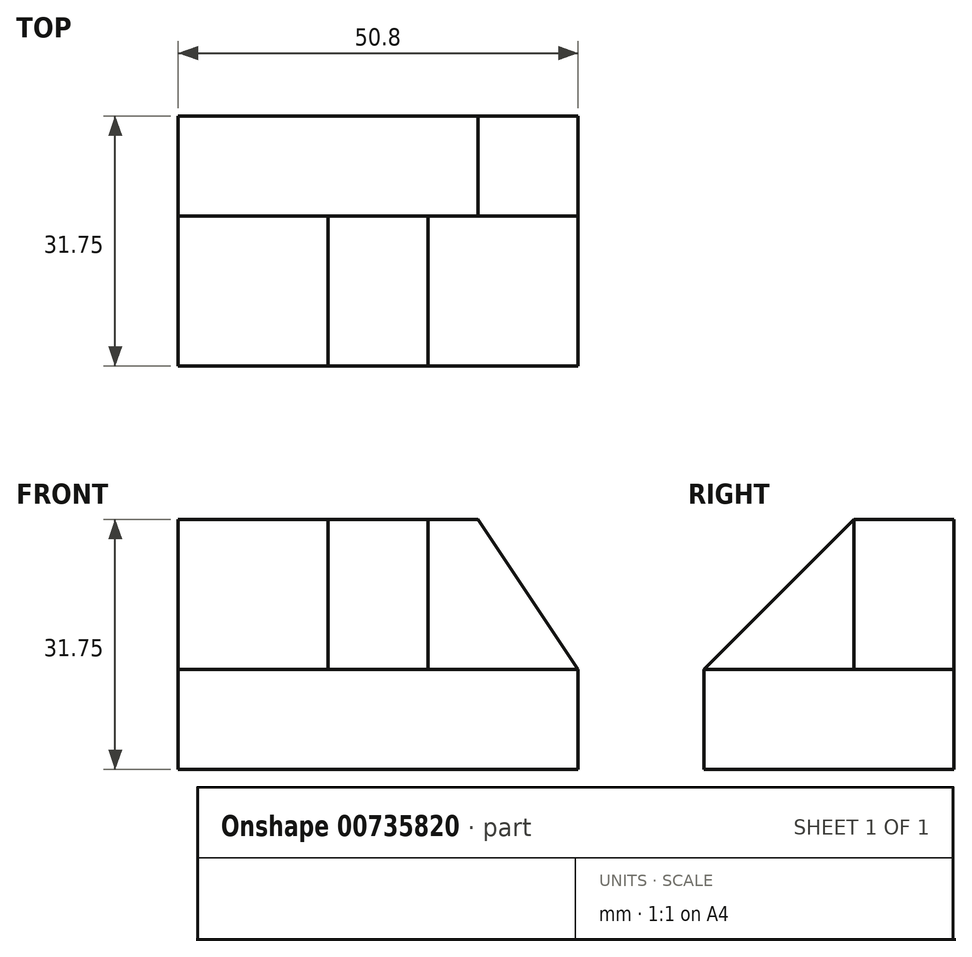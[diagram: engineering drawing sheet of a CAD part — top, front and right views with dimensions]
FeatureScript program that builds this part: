
annotation { "Feature Type Name" : "Feature", "Feature Type Description" : "" }
export const myFeature = defineFeature(function(context is Context, id is Id, definition is map)
    precondition{}
    {
        {
            var Q0;
            Q0=qCreatedBy(makeId("Front.planeOp"),FACE);
            var sketch = newSketch(context, id + "F0", { "sketchPlane" : qUnion([Q0])});
            skLineSegment(sketch, "E0", {"start": v(0, 0) * mm, "end": v(0, 12.7) * mm});
            skLineSegment(sketch, "E1", {"start": v(0, 12.7) * mm, "end": v(50.8, 12.7) * mm});
            skLineSegment(sketch, "E2", {"start": v(50.8, 12.7) * mm, "end": v(50.8, 0) * mm});
            skLineSegment(sketch, "E3", {"start": v(50.8, 0) * mm, "end": v(0, 0) * mm});
            skSolve(sketch);
        }
        {
            var Q0;
            Q0 = qSketchRegion(id + "F0", true);
            extrude(context, id + "F1", {"entities" : qUnion([Q0]), "depth" : 31.75 * mm, "offsetDistance" : 25.4 * mm});
        }
        {
            var Q0;
            Q0=makeQuery(id+"F1.opExtrude","SWEPT_FACE",FACE,{"disambiguationData":[OSD([sQuery(id+"F0.wireOp",EDGE,"E1")])]});
            var sketch = newSketch(context, id + "F2", { "sketchPlane" : qUnion([Q0])});
            skLineSegment(sketch, "E4", {"start": v(50.8, 0) * mm, "end": v(0, 0) * mm});
            skLineSegment(sketch, "E5", {"start": v(0, 0) * mm, "end": v(0, -12.7) * mm});
            skLineSegment(sketch, "E6", {"start": v(0, -12.7) * mm, "end": v(50.8, -12.7) * mm});
            skLineSegment(sketch, "E7", {"start": v(50.8, -12.7) * mm, "end": v(50.8, 0) * mm});
            skSolve(sketch);
        }
        {
            var Q0;
            Q0 = qSketchRegion(id + "F2", true);
            extrude(context, id + "F3", {"entities" : qUnion([Q0]), "operationType" : NewBodyOperationType.ADD, "depth" : 19.05 * mm, "offsetDistance" : 25.4 * mm});
        }
        {
            var Q0;
            Q0=makeQuery(id+"F3.opExtrude","SWEPT_FACE",FACE,{"disambiguationData":[OSD([sQuery(id+"F2.wireOp",EDGE,"E6")])]});
            var sketch = newSketch(context, id + "F4", { "sketchPlane" : qUnion([Q0])});
            skLineSegment(sketch, "E8", {"start": v(50.8, 12.7) * mm, "end": v(50.8, 31.75) * mm});
            skLineSegment(sketch, "E9", {"start": v(50.8, 31.75) * mm, "end": v(38.1, 31.75) * mm});
            skLineSegment(sketch, "E10", {"start": v(38.1, 31.75) * mm, "end": v(50.8, 12.7) * mm});
            skSolve(sketch);
        }
        {
            var Q0;
            Q0 = qSketchRegion(id + "F4", true);
            extrude(context, id + "F5", {"entities" : qUnion([Q0]), "operationType" : NewBodyOperationType.REMOVE, "oppositeDirection" : true, "depth" : 12.7 * mm, "offsetDistance" : 25.4 * mm});
        }
        {
            var Q0;
            Q0=makeQuery(id+"F3.opExtrude","SWEPT_FACE",FACE,{"disambiguationData":[OSD([sQuery(id+"F2.wireOp",EDGE,"E6")])]});
            var sketch = newSketch(context, id + "F6", { "sketchPlane" : qUnion([Q0])});
            skLineSegment(sketch, "E11", {"start": v(31.75, 31.75) * mm, "end": v(31.75, 12.7) * mm});
            skLineSegment(sketch, "E12", {"start": v(31.75, 12.7) * mm, "end": v(19.05, 12.7) * mm});
            skLineSegment(sketch, "E13", {"start": v(19.05, 12.7) * mm, "end": v(19.05, 31.75) * mm});
            skLineSegment(sketch, "E14", {"start": v(19.05, 31.75) * mm, "end": v(31.75, 31.75) * mm});
            skSolve(sketch);
        }
        {
            var Q0;
            Q0 = qSketchRegion(id + "F6", true);
            extrude(context, id + "F7", {"entities" : qUnion([Q0]), "operationType" : NewBodyOperationType.ADD, "depth" : 19.05 * mm, "offsetDistance" : 25.4 * mm});
        }
        {
            var Q0;
            Q0=makeQuery(id+"F7.opExtrude","SWEPT_FACE",FACE,{"disambiguationData":[OSD([sQuery(id+"F6.wireOp",EDGE,"E13")])]});
            var sketch = newSketch(context, id + "F8", { "sketchPlane" : qUnion([Q0])});
            skLineSegment(sketch, "E15", {"start": v(12.7, 31.75) * mm, "end": v(31.75, 12.7) * mm});
            skLineSegment(sketch, "E16", {"start": v(31.75, 12.7) * mm, "end": v(31.75, 31.75) * mm});
            skLineSegment(sketch, "E17", {"start": v(31.75, 31.75) * mm, "end": v(12.7, 31.75) * mm});
            skSolve(sketch);
        }
        {
            var Q0;
            Q0 = qSketchRegion(id + "F8", true);
            extrude(context, id + "F9", {"entities" : qUnion([Q0]), "operationType" : NewBodyOperationType.REMOVE, "oppositeDirection" : true, "depth" : 12.7 * mm, "offsetDistance" : 25.4 * mm});
        }
    });
